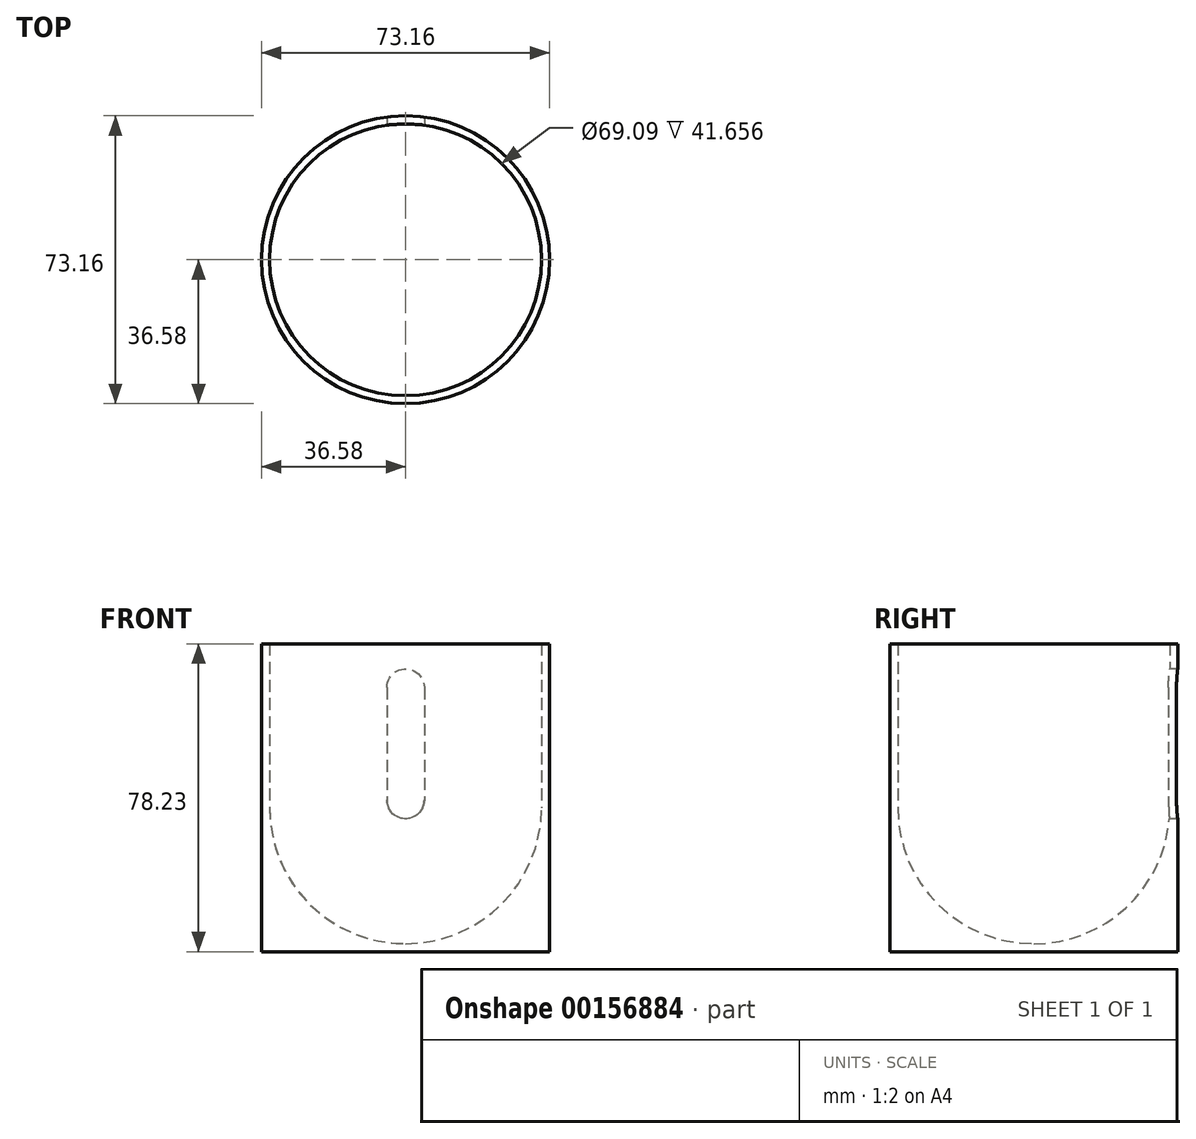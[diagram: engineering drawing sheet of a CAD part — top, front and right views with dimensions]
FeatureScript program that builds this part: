
annotation { "Feature Type Name" : "Feature", "Feature Type Description" : "" }
export const myFeature = defineFeature(function(context is Context, id is Id, definition is map)
    precondition{}
    {
        {
            var Q0;
            Q0=qCreatedBy(makeId("Front.planeOp"),FACE);
            var sketch = newSketch(context, id + "F0", { "sketchPlane" : qUnion([Q0])});
            skLineSegment(sketch, "E0", {"start": v(34.54, 78.23) * mm, "end": v(36.58, 78.23) * mm});
            skLineSegment(sketch, "E1", {"start": v(36.58, 0) * mm, "end": v(36.58, 78.23) * mm});
            skLineSegment(sketch, "E2", {"start": v(36.58, 0) * mm, "end": v(0, 0) * mm});
            skLineSegment(sketch, "E3", {"start": v(0, 0) * mm, "end": v(0, 2.03) * mm});
            skLineSegment(sketch, "E4", {"start": v(34.54, 78.23) * mm, "end": v(34.54, 36.58) * mm});
            skArc(sketch, "E5", {"start": v(0, 2.03) * mm, "mid": v(24.43, 12.15) * mm, "end": v(34.54, 36.58) * mm});
            skPoint(sketch, "E6.trimOffspring.end.orphan", {"position": v(0, 78.23) * mm});
            skSolve(sketch);
        }
        {
            var Q0;
            Q0 = qSketchRegion(id + "F0", true);
            var Q1;
            Q1=sQuery(id+"F0.wireOp",EDGE,"E3");
            revolve(context, id + "F1", {"entities" : qUnion([Q0]), "axis" : qUnion([Q1]), "revolveType" : RevolveType.FULL});
        }
        {
            var Q0;
            Q0=qCreatedBy(makeId("Front.planeOp"),FACE);
            var sketch = newSketch(context, id + "F2", { "sketchPlane" : qUnion([Q0])});
            skLineSegment(sketch, "E7", {"start": v(-4.76, 38.54) * mm, "end": v(-4.76, 67.12) * mm});
            skLineSegment(sketch, "E8", {"start": v(4.76, 67.12) * mm, "end": v(4.76, 38.54) * mm});
            skArc(sketch, "E9", {"start": v(4.76, 67.12) * mm, "mid": v(0, 71.88) * mm, "end": v(-4.76, 67.12) * mm});
            skArc(sketch, "E10", {"start": v(-4.76, 38.54) * mm, "mid": v(0, 33.78) * mm, "end": v(4.76, 38.54) * mm});
            skSolve(sketch);
        }
        {
            var Q0;
            Q0 = qSketchRegion(id + "F2", true);
            extrude(context, id + "F3", {"entities" : qUnion([Q0]), "operationType" : NewBodyOperationType.REMOVE, "endBound" : BoundingType.THROUGH_ALL, "oppositeDirection" : true, "depth" : 25.4 * mm});
        }
    });
